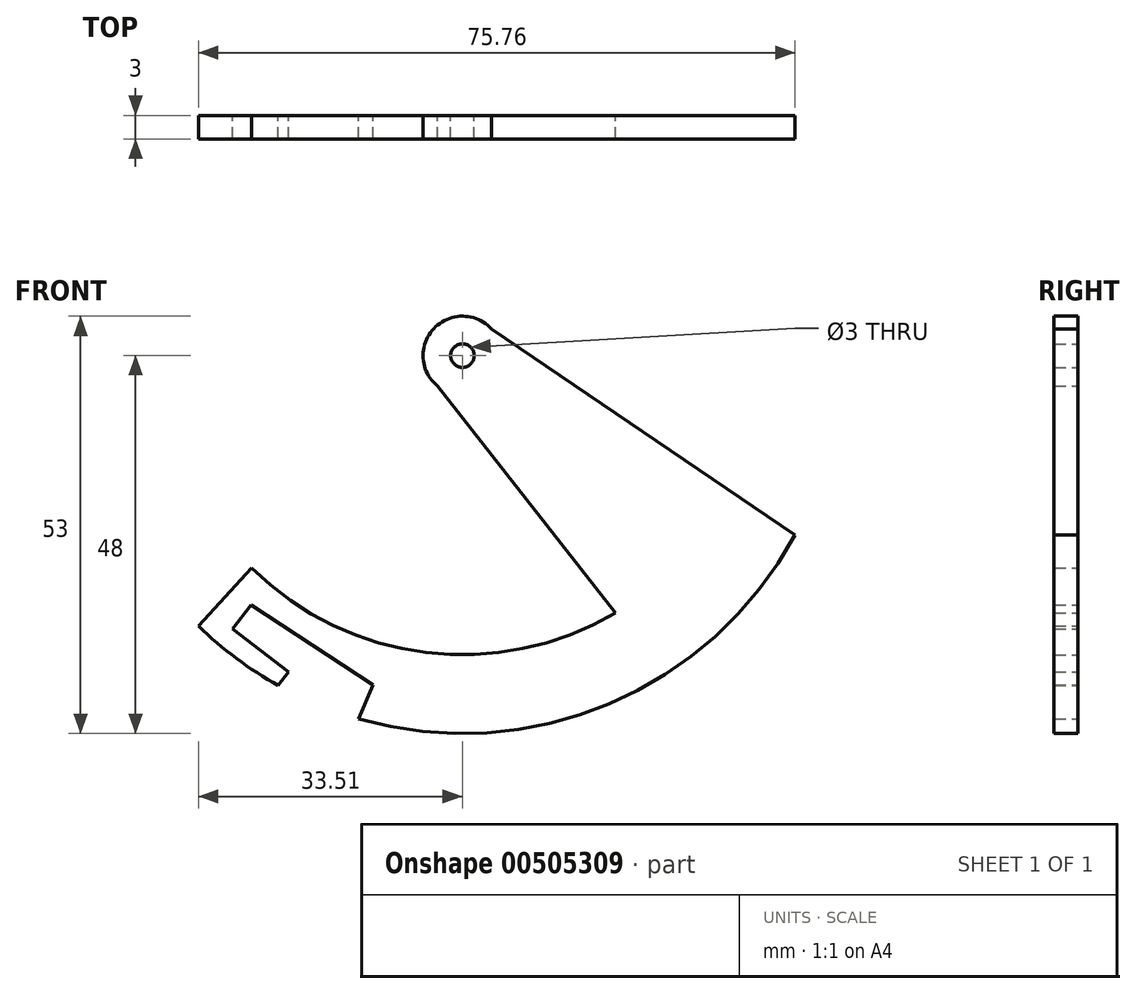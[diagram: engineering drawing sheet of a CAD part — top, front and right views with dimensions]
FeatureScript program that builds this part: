
annotation { "Feature Type Name" : "Feature", "Feature Type Description" : "" }
export const myFeature = defineFeature(function(context is Context, id is Id, definition is map)
    precondition{}
    {
        {
            var Q0;
            Q0=qCreatedBy(makeId("Front.planeOp"),FACE);
            var sketch = newSketch(context, id + "F0", { "sketchPlane" : qUnion([Q0])});
            skCircle(sketch, "E0", {"center": v(0, 0) * mm, "radius": 48 * mm});
            skCircle(sketch, "E1", {"center": v(0, 0) * mm, "radius": 1.5 * mm});
            skCircle(sketch, "E2", {"center": v(0, 0) * mm, "radius": 5 * mm});
            skLineSegment(sketch, "E3", {"start": v(3.68, 3.38) * mm, "end": v(42.25, -22.78) * mm});
            skLineSegment(sketch, "E4", {"start": v(-33.51, -34.36) * mm, "end": v(-26.76, -26.99) * mm});
            skCircle(sketch, "E5", {"center": v(0, 0) * mm, "radius": 38 * mm});
            skLineSegment(sketch, "E6", {"start": v(-3.17, -3.86) * mm, "end": v(19.42, -32.67) * mm});
            skLineSegment(sketch, "E7", {"start": v(-23.39, -41.92) * mm, "end": v(-22.08, -40.2) * mm});
            skLineSegment(sketch, "E8", {"start": v(-22.08, -40.2) * mm, "end": v(-29.2, -34.76) * mm});
            skLineSegment(sketch, "E9", {"start": v(-29.2, -34.76) * mm, "end": v(-26.86, -31.7) * mm});
            skLineSegment(sketch, "E10", {"start": v(-26.86, -31.7) * mm, "end": v(-11.35, -41.86) * mm});
            skLineSegment(sketch, "E11", {"start": v(-11.35, -41.86) * mm, "end": v(-13.2, -46.15) * mm});
            skSolve(sketch);
        }
        {
            var Q0;
            {var subQ5=sQuery(id+"F0.wireOp",EDGE,"E4");Q0=makeQuery(id+"F0.imprint","IMPRINT",FACE,{"disambiguationData":[TD([[makeQuery(id+"F0.imprint","IMPRINT",EDGE,{"derivedFrom":subQ5}),-1.0]])]});}
            var Q1;
            {var subQ0=sQuery(id+"F0.wireOp",EDGE,"E3");var subQ1=sQuery(id+"F0.wireOp",EDGE,"E2");var subQ2=makeQuery(id+"F0.imprint","INTERSECT",VERTEX,{"derivedFrom":[subQ1,subQ0]});Q1=makeQuery(id+"F0.imprint","IMPRINT",FACE,{"disambiguationData":[TD([[makeQuery(id+"F0.imprint","IMPRINT",EDGE,{"disambiguationData":[TD([[subQ2,1.0]])],"derivedFrom":subQ1}),-1.0]])]});}
            var Q2;
            Q2=makeQuery(id+"F0.imprint","IMPRINT",FACE,{"disambiguationData":[TD([[makeQuery(id+"F0.imprint","IMPRINT",EDGE,{"derivedFrom":sQuery(id+"F0.wireOp",EDGE,"E1")}),-1.0]])]});
            extrude(context, id + "F1", {"entities" : qUnion([Q0, Q1, Q2]), "depth" : 3 * mm});
        }
    });
